# Revit family: QF_ADVENTYS_ADV1835-B_IE-F-DIR_1000
name_source: partatom
category: Attrezzature speciali
units: mm (PartAtom-declared; Revit-internal decimal feet)

## family parameters
Condiviso = No
Host = Superficie
Punto di calcolo locali = No
Quota connettore circolare = Usa diametro
Taglio con vuoti quando caricato = No
Tipo di parte = Normale

## types (1)
- ADV1835-B
    Controller_Height = 98 mm  [stored 0.321522 ft]
    Controller_Width = 228 mm  [stored 0.748031 ft]
    Cycle = 50 Hz
    Depth = 340 mm  [stored 1.11549 ft]
    Depth Actual = 280 mm  [stored 0.918635 ft]
    Height = 172 mm  [stored 0.564304 ft]
    Height Actual = 94 mm  [stored 0.308399 ft]
    Item Number = ADV1835-B
    Length Actual = 280 mm  [stored 0.918635 ft]
    Modello = IE-F-DIR 1000
    Phase = 1
    Produttore = ADVENTYS
    Prospetto di default = 1219.2 mm  [stored 4 ft]
    URL = https://adventys.com
    Volts = 220 V
    Watts = 1000 W
    Weight = 4.5
    Width = 340 mm  [stored 1.11549 ft]

note: [stored X ft] marks values corroborated as IEEE doubles in the binary element streams (Revit-internal decimal feet)
